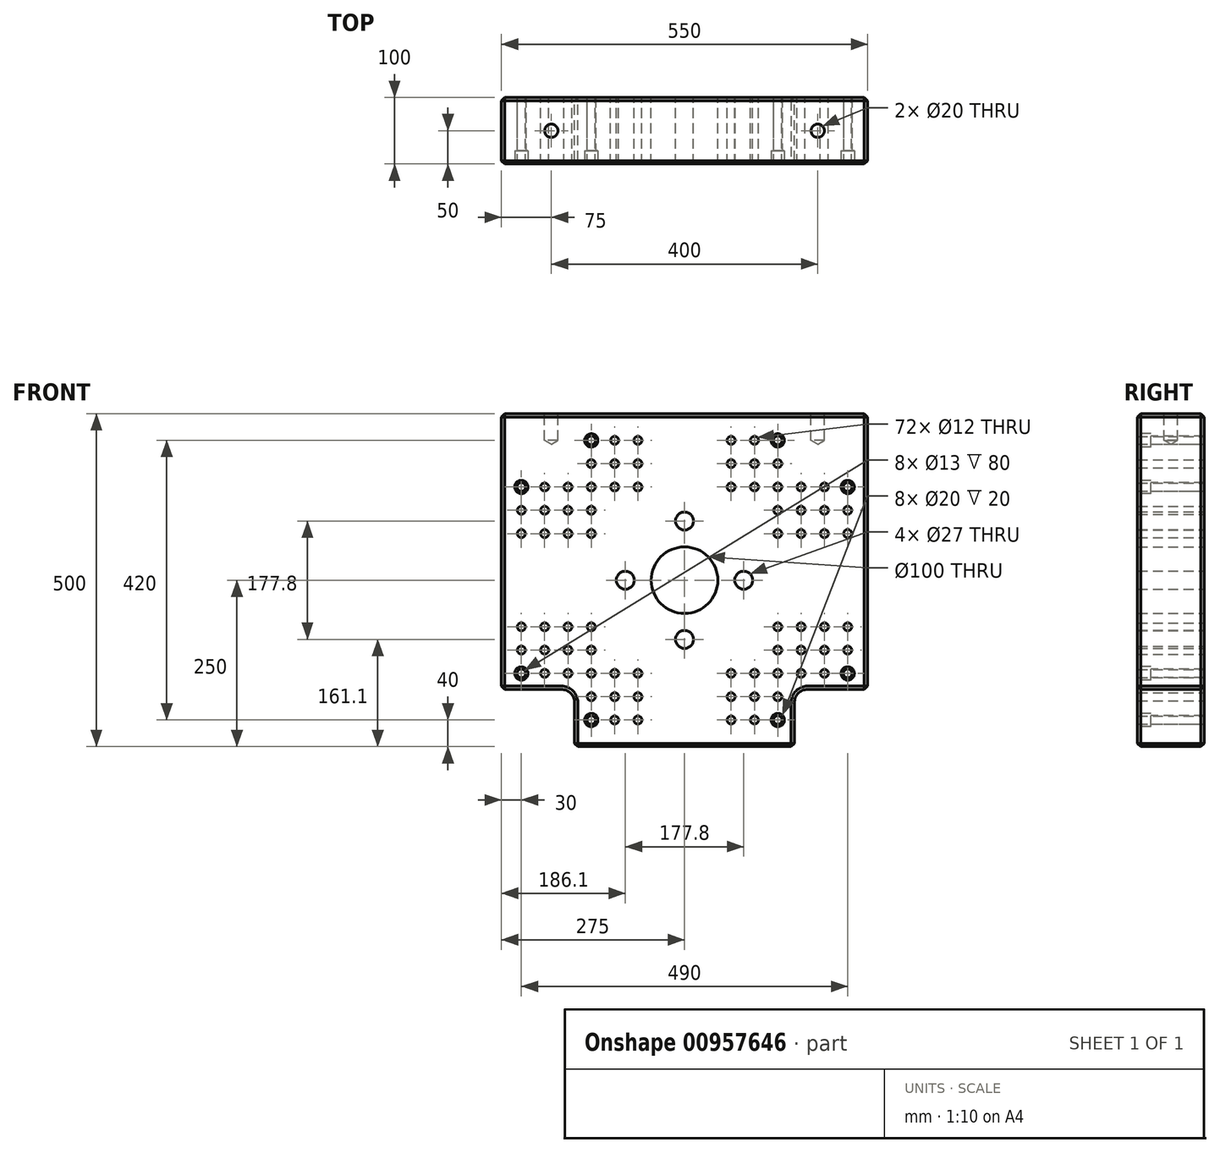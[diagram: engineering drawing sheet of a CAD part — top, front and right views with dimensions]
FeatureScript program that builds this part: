
annotation { "Feature Type Name" : "Feature", "Feature Type Description" : "" }
export const myFeature = defineFeature(function(context is Context, id is Id, definition is map)
    precondition{}
    {
        {
            var Q0;
            Q0=qCreatedBy(makeId("Front.planeOp"),FACE);
            var sketch = newSketch(context, id + "F0", { "sketchPlane" : qUnion([Q0])});
            skLineSegment(sketch, "E0", {"start": v(0, 0) * mm, "end": v(-219.59, 0) * mm, "construction": true});
            skLineSegment(sketch, "E1", {"start": v(0, 0) * mm, "end": v(0, -187.77) * mm, "construction": true});
            skLineSegment(sketch, "E2", {"start": v(-275, 250) * mm, "end": v(-275, -164) * mm});
            skLineSegment(sketch, "E3", {"start": v(-165, -250) * mm, "end": v(165, -250) * mm});
            skLineSegment(sketch, "E4", {"start": v(275, -164) * mm, "end": v(275, 250) * mm});
            skLineSegment(sketch, "E5", {"start": v(275, 250) * mm, "end": v(-275, 250) * mm});
            skLineSegment(sketch, "E6", {"start": v(-275, -164) * mm, "end": v(-185, -164) * mm});
            skLineSegment(sketch, "E7", {"start": v(-165, -184) * mm, "end": v(-165, -250) * mm});
            skLineSegment(sketch, "E8", {"start": v(165, -250) * mm, "end": v(165, -184) * mm});
            skLineSegment(sketch, "E9", {"start": v(185, -164) * mm, "end": v(275, -164) * mm});
            skCircle(sketch, "E10", {"center": v(0, 0) * mm, "radius": 50 * mm});
            skCircle(sketch, "E11", {"center": v(-140, 210) * mm, "radius": 6 * mm});
            skCircle(sketch, "E12.0.1.0", {"center": v(-140, 175) * mm, "radius": 6 * mm});
            skCircle(sketch, "E12.0.2.0", {"center": v(-140, 140) * mm, "radius": 6 * mm});
            skCircle(sketch, "E12.1.0.0", {"center": v(-105, 210) * mm, "radius": 6 * mm});
            skCircle(sketch, "E12.1.1.0", {"center": v(-105, 175) * mm, "radius": 6 * mm});
            skCircle(sketch, "E12.1.2.0", {"center": v(-105, 140) * mm, "radius": 6 * mm});
            skCircle(sketch, "E12.2.0.0", {"center": v(-70, 210) * mm, "radius": 6 * mm});
            skCircle(sketch, "E12.2.1.0", {"center": v(-70, 175) * mm, "radius": 6 * mm});
            skCircle(sketch, "E12.2.2.0", {"center": v(-70, 140) * mm, "radius": 6 * mm});
            skLineSegment(sketch, "E12.direction1", {"start": v(-140, 210) * mm, "end": v(-105, 210) * mm, "construction": true});
            skLineSegment(sketch, "E12.direction2", {"start": v(-140, 210) * mm, "end": v(-140, 175) * mm, "construction": true});
            skCircle(sketch, "E13.0.1.0", {"center": v(-140, 105) * mm, "radius": 6 * mm});
            skCircle(sketch, "E13.0.2.0", {"center": v(-140, 70) * mm, "radius": 6 * mm});
            skCircle(sketch, "E13.1.0.0", {"center": v(-175, 140) * mm, "radius": 6 * mm});
            skCircle(sketch, "E13.1.1.0", {"center": v(-175, 105) * mm, "radius": 6 * mm});
            skCircle(sketch, "E13.1.2.0", {"center": v(-175, 70) * mm, "radius": 6 * mm});
            skCircle(sketch, "E13.2.0.0", {"center": v(-210, 140) * mm, "radius": 6 * mm});
            skCircle(sketch, "E13.2.1.0", {"center": v(-210, 105) * mm, "radius": 6 * mm});
            skCircle(sketch, "E13.2.2.0", {"center": v(-210, 70) * mm, "radius": 6 * mm});
            skCircle(sketch, "E13.3.0.0", {"center": v(-245, 140) * mm, "radius": 6 * mm});
            skCircle(sketch, "E13.3.1.0", {"center": v(-245, 105) * mm, "radius": 6 * mm});
            skCircle(sketch, "E13.3.2.0", {"center": v(-245, 70) * mm, "radius": 6 * mm});
            skLineSegment(sketch, "E13.direction1", {"start": v(-140, 140) * mm, "end": v(-175, 140) * mm, "construction": true});
            skLineSegment(sketch, "E13.direction2", {"start": v(-140, 140) * mm, "end": v(-140, 105) * mm, "construction": true});
            skCircle(sketch, "E14.MirrorC", {"center": v(140, 210) * mm, "radius": 6 * mm});
            skCircle(sketch, "E15.MirrorC", {"center": v(140, 140) * mm, "radius": 6 * mm});
            skCircle(sketch, "E16.MirrorC", {"center": v(140, 175) * mm, "radius": 6 * mm});
            skCircle(sketch, "E17.MirrorC", {"center": v(140, 105) * mm, "radius": 6 * mm});
            skCircle(sketch, "E18.MirrorC", {"center": v(105, 210) * mm, "radius": 6 * mm});
            skCircle(sketch, "E19.MirrorC", {"center": v(175, 140) * mm, "radius": 6 * mm});
            skCircle(sketch, "E20.MirrorC", {"center": v(105, 140) * mm, "radius": 6 * mm});
            skCircle(sketch, "E21.MirrorC", {"center": v(105, 175) * mm, "radius": 6 * mm});
            skCircle(sketch, "E22.MirrorC", {"center": v(210, 105) * mm, "radius": 6 * mm});
            skCircle(sketch, "E23.MirrorC", {"center": v(210, 70) * mm, "radius": 6 * mm});
            skCircle(sketch, "E24.MirrorC", {"center": v(175, 105) * mm, "radius": 6 * mm});
            skCircle(sketch, "E25.MirrorC", {"center": v(70, 210) * mm, "radius": 6 * mm});
            skCircle(sketch, "E26.MirrorC", {"center": v(245, 70) * mm, "radius": 6 * mm});
            skCircle(sketch, "E27.MirrorC", {"center": v(210, 140) * mm, "radius": 6 * mm});
            skCircle(sketch, "E28.MirrorC", {"center": v(245, 140) * mm, "radius": 6 * mm});
            skCircle(sketch, "E29.MirrorC", {"center": v(140, 70) * mm, "radius": 6 * mm});
            skCircle(sketch, "E30.MirrorC", {"center": v(70, 175) * mm, "radius": 6 * mm});
            skCircle(sketch, "E31.MirrorC", {"center": v(175, 70) * mm, "radius": 6 * mm});
            skCircle(sketch, "E32.MirrorC", {"center": v(245, 105) * mm, "radius": 6 * mm});
            skCircle(sketch, "E33.MirrorC", {"center": v(70, 140) * mm, "radius": 6 * mm});
            skLineSegment(sketch, "E34.MirrorCS", {"start": v(140, 140) * mm, "end": v(140, 105) * mm, "construction": true});
            skLineSegment(sketch, "E35.MirrorCS", {"start": v(140, 140) * mm, "end": v(175, 140) * mm, "construction": true});
            skLineSegment(sketch, "E36.MirrorCS", {"start": v(140, 210) * mm, "end": v(140, 175) * mm, "construction": true});
            skLineSegment(sketch, "E37.MirrorCS", {"start": v(140, 210) * mm, "end": v(105, 210) * mm, "construction": true});
            skCircle(sketch, "E38.MirrorC", {"center": v(-140, -210) * mm, "radius": 6 * mm});
            skCircle(sketch, "E39.MirrorC", {"center": v(-140, -140) * mm, "radius": 6 * mm});
            skCircle(sketch, "E40.MirrorC", {"center": v(140, -140) * mm, "radius": 6 * mm});
            skCircle(sketch, "E41.MirrorC", {"center": v(140, -210) * mm, "radius": 6 * mm});
            skCircle(sketch, "E42.MirrorC", {"center": v(-175, -140) * mm, "radius": 6 * mm});
            skCircle(sketch, "E43.MirrorC", {"center": v(105, -210) * mm, "radius": 6 * mm});
            skCircle(sketch, "E44.MirrorC", {"center": v(-105, -210) * mm, "radius": 6 * mm});
            skCircle(sketch, "E45.MirrorC", {"center": v(140, -105) * mm, "radius": 6 * mm});
            skCircle(sketch, "E46.MirrorC", {"center": v(140, -175) * mm, "radius": 6 * mm});
            skCircle(sketch, "E47.MirrorC", {"center": v(175, -140) * mm, "radius": 6 * mm});
            skCircle(sketch, "E48.MirrorC", {"center": v(-140, -105) * mm, "radius": 6 * mm});
            skCircle(sketch, "E49.MirrorC", {"center": v(-140, -175) * mm, "radius": 6 * mm});
            skCircle(sketch, "E50.MirrorC", {"center": v(245, -105) * mm, "radius": 6 * mm});
            skLineSegment(sketch, "E51.MirrorCS", {"start": v(-140, -210) * mm, "end": v(-105, -210) * mm, "construction": true});
            skCircle(sketch, "E52.MirrorC", {"center": v(-175, -70) * mm, "radius": 6 * mm});
            skCircle(sketch, "E53.MirrorC", {"center": v(-210, -140) * mm, "radius": 6 * mm});
            skCircle(sketch, "E54.MirrorC", {"center": v(70, -175) * mm, "radius": 6 * mm});
            skCircle(sketch, "E55.MirrorC", {"center": v(-105, -140) * mm, "radius": 6 * mm});
            skCircle(sketch, "E56.MirrorC", {"center": v(175, -105) * mm, "radius": 6 * mm});
            skCircle(sketch, "E57.MirrorC", {"center": v(-105, -175) * mm, "radius": 6 * mm});
            skCircle(sketch, "E58.MirrorC", {"center": v(105, -140) * mm, "radius": 6 * mm});
            skCircle(sketch, "E59.MirrorC", {"center": v(-175, -105) * mm, "radius": 6 * mm});
            skCircle(sketch, "E60.MirrorC", {"center": v(245, -140) * mm, "radius": 6 * mm});
            skCircle(sketch, "E61.MirrorC", {"center": v(-245, -140) * mm, "radius": 6 * mm});
            skCircle(sketch, "E62.MirrorC", {"center": v(70, -140) * mm, "radius": 6 * mm});
            skCircle(sketch, "E63.MirrorC", {"center": v(-70, -175) * mm, "radius": 6 * mm});
            skCircle(sketch, "E64.MirrorC", {"center": v(-210, -105) * mm, "radius": 6 * mm});
            skCircle(sketch, "E65.MirrorC", {"center": v(70, -210) * mm, "radius": 6 * mm});
            skCircle(sketch, "E66.MirrorC", {"center": v(-70, -210) * mm, "radius": 6 * mm});
            skCircle(sketch, "E67.MirrorC", {"center": v(-140, -70) * mm, "radius": 6 * mm});
            skCircle(sketch, "E68.MirrorC", {"center": v(-245, -105) * mm, "radius": 6 * mm});
            skCircle(sketch, "E69.MirrorC", {"center": v(245, -70) * mm, "radius": 6 * mm});
            skCircle(sketch, "E70.MirrorC", {"center": v(175, -70) * mm, "radius": 6 * mm});
            skCircle(sketch, "E71.MirrorC", {"center": v(-245, -70) * mm, "radius": 6 * mm});
            skCircle(sketch, "E72.MirrorC", {"center": v(210, -140) * mm, "radius": 6 * mm});
            skCircle(sketch, "E73.MirrorC", {"center": v(210, -70) * mm, "radius": 6 * mm});
            skCircle(sketch, "E74.MirrorC", {"center": v(-70, -140) * mm, "radius": 6 * mm});
            skCircle(sketch, "E75.MirrorC", {"center": v(210, -105) * mm, "radius": 6 * mm});
            skCircle(sketch, "E76.MirrorC", {"center": v(140, -70) * mm, "radius": 6 * mm});
            skCircle(sketch, "E77.MirrorC", {"center": v(-210, -70) * mm, "radius": 6 * mm});
            skCircle(sketch, "E78.MirrorC", {"center": v(105, -175) * mm, "radius": 6 * mm});
            skLineSegment(sketch, "E79.MirrorCS", {"start": v(-140, -140) * mm, "end": v(-175, -140) * mm, "construction": true});
            skLineSegment(sketch, "E80.MirrorCS", {"start": v(-140, -210) * mm, "end": v(-140, -175) * mm, "construction": true});
            skLineSegment(sketch, "E81.MirrorCS", {"start": v(140, -210) * mm, "end": v(105, -210) * mm, "construction": true});
            skLineSegment(sketch, "E82.MirrorCS", {"start": v(140, -140) * mm, "end": v(140, -105) * mm, "construction": true});
            skLineSegment(sketch, "E83.MirrorCS", {"start": v(140, -210) * mm, "end": v(140, -175) * mm, "construction": true});
            skLineSegment(sketch, "E84.MirrorCS", {"start": v(-140, -140) * mm, "end": v(-140, -105) * mm, "construction": true});
            skLineSegment(sketch, "E85.MirrorCS", {"start": v(140, -140) * mm, "end": v(175, -140) * mm, "construction": true});
            skPoint(sketch, "E86.visualSharp", {"position": v(-165, -164) * mm});
            skArc(sketch, "E86.filletArc", {"start": v(-165, -184) * mm, "mid": v(-170.86, -169.86) * mm, "end": v(-185, -164) * mm});
            skPoint(sketch, "E87.visualSharp", {"position": v(165, -164) * mm});
            skArc(sketch, "E87.filletArc", {"start": v(185, -164) * mm, "mid": v(170.86, -169.86) * mm, "end": v(165, -184) * mm});
            skCircle(sketch, "E88", {"center": v(88.9, 0) * mm, "radius": 13.5 * mm});
            skCircle(sketch, "E89", {"center": v(0, 88.9) * mm, "radius": 13.5 * mm});
            skCircle(sketch, "E90", {"center": v(-88.9, 0) * mm, "radius": 13.5 * mm});
            skCircle(sketch, "E91", {"center": v(0, -88.9) * mm, "radius": 13.5 * mm});
            skSolve(sketch);
        }
        {
            var Q0;
            Q0 = qSketchRegion(id + "F0", true);
            extrude(context, id + "F1", {"entities" : qUnion([Q0]), "depth" : 100 * mm, "offsetDistance" : 25 * mm});
        }
        {
            var Q0;
            Q0=makeQuery(id+"F1.opExtrude","CAP_FACE",FACE,{"disambiguationData":[OSD([sQuery(id+"F0.wireOp",EDGE,"E2"),sQuery(id+"F0.wireOp",EDGE,"E3"),sQuery(id+"F0.wireOp",EDGE,"E4"),sQuery(id+"F0.wireOp",EDGE,"E5"),sQuery(id+"F0.wireOp",EDGE,"E6"),sQuery(id+"F0.wireOp",EDGE,"E7"),sQuery(id+"F0.wireOp",EDGE,"E8"),sQuery(id+"F0.wireOp",EDGE,"E9"),sQuery(id+"F0.wireOp",EDGE,"E10"),sQuery(id+"F0.wireOp",EDGE,"E11"),sQuery(id+"F0.wireOp",EDGE,"E12.0.1.0"),sQuery(id+"F0.wireOp",EDGE,"E12.0.2.0"),sQuery(id+"F0.wireOp",EDGE,"E12.1.0.0"),sQuery(id+"F0.wireOp",EDGE,"E12.1.1.0"),sQuery(id+"F0.wireOp",EDGE,"E12.1.2.0"),sQuery(id+"F0.wireOp",EDGE,"E12.2.0.0"),sQuery(id+"F0.wireOp",EDGE,"E12.2.1.0"),sQuery(id+"F0.wireOp",EDGE,"E12.2.2.0"),sQuery(id+"F0.wireOp",EDGE,"E13.0.1.0"),sQuery(id+"F0.wireOp",EDGE,"E13.0.2.0"),sQuery(id+"F0.wireOp",EDGE,"E13.0.3.0"),sQuery(id+"F0.wireOp",EDGE,"E13.1.0.0"),sQuery(id+"F0.wireOp",EDGE,"E13.1.1.0"),sQuery(id+"F0.wireOp",EDGE,"E13.1.2.0"),sQuery(id+"F0.wireOp",EDGE,"E13.1.3.0"),sQuery(id+"F0.wireOp",EDGE,"E13.2.0.0"),sQuery(id+"F0.wireOp",EDGE,"E13.2.1.0"),sQuery(id+"F0.wireOp",EDGE,"E13.2.2.0"),sQuery(id+"F0.wireOp",EDGE,"E13.2.3.0"),sQuery(id+"F0.wireOp",EDGE,"E13.3.0.0"),sQuery(id+"F0.wireOp",EDGE,"E13.3.1.0"),sQuery(id+"F0.wireOp",EDGE,"E13.3.2.0"),sQuery(id+"F0.wireOp",EDGE,"E13.3.3.0"),sQuery(id+"F0.wireOp",EDGE,"E14.MirrorC"),sQuery(id+"F0.wireOp",EDGE,"E15.MirrorC"),sQuery(id+"F0.wireOp",EDGE,"E16.MirrorC"),sQuery(id+"F0.wireOp",EDGE,"E17.MirrorC"),sQuery(id+"F0.wireOp",EDGE,"E18.MirrorC"),sQuery(id+"F0.wireOp",EDGE,"E19.MirrorC"),sQuery(id+"F0.wireOp",EDGE,"97c1720e-c5f1-4ad0-973d-ed2b327d89556.MirrorC"),sQuery(id+"F0.wireOp",EDGE,"E20.MirrorC"),sQuery(id+"F0.wireOp",EDGE,"97c1720e-c5f1-4ad0-973d-ed2b327d89558.MirrorC"),sQuery(id+"F0.wireOp",EDGE,"E21.MirrorC"),sQuery(id+"F0.wireOp",EDGE,"E150.MirrorC"),sQuery(id+"F0.wireOp",EDGE,"E22.MirrorC"),sQuery(id+"F0.wireOp",EDGE,"E23.MirrorC"),sQuery(id+"F0.wireOp",EDGE,"E24.MirrorC"),sQuery(id+"F0.wireOp",EDGE,"E25.MirrorC"),sQuery(id+"F0.wireOp",EDGE,"E26.MirrorC"),sQuery(id+"F0.wireOp",EDGE,"E27.MirrorC"),sQuery(id+"F0.wireOp",EDGE,"E28.MirrorC"),sQuery(id+"F0.wireOp",EDGE,"E29.MirrorC"),sQuery(id+"F0.wireOp",EDGE,"E30.MirrorC"),sQuery(id+"F0.wireOp",EDGE,"E160.MirrorC"),sQuery(id+"F0.wireOp",EDGE,"E31.MirrorC"),sQuery(id+"F0.wireOp",EDGE,"E32.MirrorC"),sQuery(id+"F0.wireOp",EDGE,"E33.MirrorC"),sQuery(id+"F0.wireOp",EDGE,"E38.MirrorC"),sQuery(id+"F0.wireOp",EDGE,"E39.MirrorC"),sQuery(id+"F0.wireOp",EDGE,"E40.MirrorC"),sQuery(id+"F0.wireOp",EDGE,"E41.MirrorC"),sQuery(id+"F0.wireOp",EDGE,"E42.MirrorC"),sQuery(id+"F0.wireOp",EDGE,"E43.MirrorC"),sQuery(id+"F0.wireOp",EDGE,"E44.MirrorC"),sQuery(id+"F0.wireOp",EDGE,"E45.MirrorC"),sQuery(id+"F0.wireOp",EDGE,"E46.MirrorC"),sQuery(id+"F0.wireOp",EDGE,"E47.MirrorC"),sQuery(id+"F0.wireOp",EDGE,"E48.MirrorC"),sQuery(id+"F0.wireOp",EDGE,"E49.MirrorC"),sQuery(id+"F0.wireOp",EDGE,"E50.MirrorC"),sQuery(id+"F0.wireOp",EDGE,"E52.MirrorC"),sQuery(id+"F0.wireOp",EDGE,"E395.MirrorC"),sQuery(id+"F0.wireOp",EDGE,"E396.MirrorC"),sQuery(id+"F0.wireOp",EDGE,"E53.MirrorC"),sQuery(id+"F0.wireOp",EDGE,"E398.MirrorC"),sQuery(id+"F0.wireOp",EDGE,"E54.MirrorC"),sQuery(id+"F0.wireOp",EDGE,"E55.MirrorC"),sQuery(id+"F0.wireOp",EDGE,"E56.MirrorC"),sQuery(id+"F0.wireOp",EDGE,"E57.MirrorC"),sQuery(id+"F0.wireOp",EDGE,"E403.MirrorC"),sQuery(id+"F0.wireOp",EDGE,"E58.MirrorC"),sQuery(id+"F0.wireOp",EDGE,"E59.MirrorC"),sQuery(id+"F0.wireOp",EDGE,"E60.MirrorC"),sQuery(id+"F0.wireOp",EDGE,"E61.MirrorC"),sQuery(id+"F0.wireOp",EDGE,"E62.MirrorC"),sQuery(id+"F0.wireOp",EDGE,"E63.MirrorC"),sQuery(id+"F0.wireOp",EDGE,"E64.MirrorC"),sQuery(id+"F0.wireOp",EDGE,"E65.MirrorC"),sQuery(id+"F0.wireOp",EDGE,"E66.MirrorC"),sQuery(id+"F0.wireOp",EDGE,"E67.MirrorC"),sQuery(id+"F0.wireOp",EDGE,"E68.MirrorC"),sQuery(id+"F0.wireOp",EDGE,"E69.MirrorC"),sQuery(id+"F0.wireOp",EDGE,"E416.MirrorC"),sQuery(id+"F0.wireOp",EDGE,"E70.MirrorC"),sQuery(id+"F0.wireOp",EDGE,"E418.MirrorC"),sQuery(id+"F0.wireOp",EDGE,"E419.MirrorC"),sQuery(id+"F0.wireOp",EDGE,"E71.MirrorC"),sQuery(id+"F0.wireOp",EDGE,"E72.MirrorC"),sQuery(id+"F0.wireOp",EDGE,"E73.MirrorC"),sQuery(id+"F0.wireOp",EDGE,"E423.MirrorC"),sQuery(id+"F0.wireOp",EDGE,"E74.MirrorC"),sQuery(id+"F0.wireOp",EDGE,"E75.MirrorC"),sQuery(id+"F0.wireOp",EDGE,"E76.MirrorC"),sQuery(id+"F0.wireOp",EDGE,"E77.MirrorC"),sQuery(id+"F0.wireOp",EDGE,"E78.MirrorC"),sQuery(id+"F0.wireOp",EDGE,"E86.filletArc"),sQuery(id+"F0.wireOp",EDGE,"E87.filletArc"),sQuery(id+"F0.wireOp",EDGE,"E88"),sQuery(id+"F0.wireOp",EDGE,"E89"),sQuery(id+"F0.wireOp",EDGE,"E90"),sQuery(id+"F0.wireOp",EDGE,"E91")])],"isStart":false});
            var sketch = newSketch(context, id + "F2", { "sketchPlane" : qUnion([Q0])});
            skPoint(sketch, "E92", {"position": v(-245, 140) * mm});
            skPoint(sketch, "E93", {"position": v(-245, -140) * mm});
            skPoint(sketch, "E94", {"position": v(245, -140) * mm});
            skPoint(sketch, "E95", {"position": v(245, 140) * mm});
            skPoint(sketch, "E96", {"position": v(-140, 210) * mm});
            skPoint(sketch, "E97", {"position": v(70, 210) * mm});
            skPoint(sketch, "E98", {"position": v(-140, -210) * mm});
            skPoint(sketch, "E99", {"position": v(140, -210) * mm});
            skPoint(sketch, "E100", {"position": v(140, 210) * mm});
            skSolve(sketch);
        }
        {
            var Q0;
            Q0=sQuery(id+"F2.wireOp",VERTEX,"E92");
            var Q1;
            Q1=sQuery(id+"F2.wireOp",VERTEX,"E95");
            var Q2;
            Q2=sQuery(id+"F2.wireOp",VERTEX,"E94");
            var Q3;
            Q3=sQuery(id+"F2.wireOp",VERTEX,"E93");
            var Q4;
            Q4=sQuery(id+"F2.wireOp",VERTEX,"E96");
            var Q5;
            Q5=sQuery(id+"F2.wireOp",VERTEX,"E99");
            var Q6;
            Q6=sQuery(id+"F2.wireOp",VERTEX,"E98");
            var Q7;
            Q7=sQuery(id+"F2.wireOp",VERTEX,"E100");
            var Q8;
            Q8=makeQuery(id+"F1.opExtrude","SWEPT_BODY",BODY,{"disambiguationData":[OSD([sQuery(id+"F0.wireOp",EDGE,"E2"),sQuery(id+"F0.wireOp",EDGE,"E3"),sQuery(id+"F0.wireOp",EDGE,"E4"),sQuery(id+"F0.wireOp",EDGE,"E5"),sQuery(id+"F0.wireOp",EDGE,"E6"),sQuery(id+"F0.wireOp",EDGE,"E7"),sQuery(id+"F0.wireOp",EDGE,"E8"),sQuery(id+"F0.wireOp",EDGE,"E9"),sQuery(id+"F0.wireOp",EDGE,"E10"),sQuery(id+"F0.wireOp",EDGE,"E11"),sQuery(id+"F0.wireOp",EDGE,"E12.0.1.0"),sQuery(id+"F0.wireOp",EDGE,"E12.0.2.0"),sQuery(id+"F0.wireOp",EDGE,"E12.1.0.0"),sQuery(id+"F0.wireOp",EDGE,"E12.1.1.0"),sQuery(id+"F0.wireOp",EDGE,"E12.1.2.0"),sQuery(id+"F0.wireOp",EDGE,"E12.2.0.0"),sQuery(id+"F0.wireOp",EDGE,"E12.2.1.0"),sQuery(id+"F0.wireOp",EDGE,"E12.2.2.0"),sQuery(id+"F0.wireOp",EDGE,"E13.0.1.0"),sQuery(id+"F0.wireOp",EDGE,"E13.0.2.0"),sQuery(id+"F0.wireOp",EDGE,"E13.0.3.0"),sQuery(id+"F0.wireOp",EDGE,"E13.1.0.0"),sQuery(id+"F0.wireOp",EDGE,"E13.1.1.0"),sQuery(id+"F0.wireOp",EDGE,"E13.1.2.0"),sQuery(id+"F0.wireOp",EDGE,"E13.1.3.0"),sQuery(id+"F0.wireOp",EDGE,"E13.2.0.0"),sQuery(id+"F0.wireOp",EDGE,"E13.2.1.0"),sQuery(id+"F0.wireOp",EDGE,"E13.2.2.0"),sQuery(id+"F0.wireOp",EDGE,"E13.2.3.0"),sQuery(id+"F0.wireOp",EDGE,"E13.3.0.0"),sQuery(id+"F0.wireOp",EDGE,"E13.3.1.0"),sQuery(id+"F0.wireOp",EDGE,"E13.3.2.0"),sQuery(id+"F0.wireOp",EDGE,"E13.3.3.0"),sQuery(id+"F0.wireOp",EDGE,"E14.MirrorC"),sQuery(id+"F0.wireOp",EDGE,"E15.MirrorC"),sQuery(id+"F0.wireOp",EDGE,"E16.MirrorC"),sQuery(id+"F0.wireOp",EDGE,"E17.MirrorC"),sQuery(id+"F0.wireOp",EDGE,"E18.MirrorC"),sQuery(id+"F0.wireOp",EDGE,"E19.MirrorC"),sQuery(id+"F0.wireOp",EDGE,"97c1720e-c5f1-4ad0-973d-ed2b327d89556.MirrorC"),sQuery(id+"F0.wireOp",EDGE,"E20.MirrorC"),sQuery(id+"F0.wireOp",EDGE,"97c1720e-c5f1-4ad0-973d-ed2b327d89558.MirrorC"),sQuery(id+"F0.wireOp",EDGE,"E21.MirrorC"),sQuery(id+"F0.wireOp",EDGE,"E150.MirrorC"),sQuery(id+"F0.wireOp",EDGE,"E22.MirrorC"),sQuery(id+"F0.wireOp",EDGE,"E23.MirrorC"),sQuery(id+"F0.wireOp",EDGE,"E24.MirrorC"),sQuery(id+"F0.wireOp",EDGE,"E25.MirrorC"),sQuery(id+"F0.wireOp",EDGE,"E26.MirrorC"),sQuery(id+"F0.wireOp",EDGE,"E27.MirrorC"),sQuery(id+"F0.wireOp",EDGE,"E28.MirrorC"),sQuery(id+"F0.wireOp",EDGE,"E29.MirrorC"),sQuery(id+"F0.wireOp",EDGE,"E30.MirrorC"),sQuery(id+"F0.wireOp",EDGE,"E160.MirrorC"),sQuery(id+"F0.wireOp",EDGE,"E31.MirrorC"),sQuery(id+"F0.wireOp",EDGE,"E32.MirrorC"),sQuery(id+"F0.wireOp",EDGE,"E33.MirrorC"),sQuery(id+"F0.wireOp",EDGE,"E38.MirrorC"),sQuery(id+"F0.wireOp",EDGE,"E39.MirrorC"),sQuery(id+"F0.wireOp",EDGE,"E40.MirrorC"),sQuery(id+"F0.wireOp",EDGE,"E41.MirrorC"),sQuery(id+"F0.wireOp",EDGE,"E42.MirrorC"),sQuery(id+"F0.wireOp",EDGE,"E43.MirrorC"),sQuery(id+"F0.wireOp",EDGE,"E44.MirrorC"),sQuery(id+"F0.wireOp",EDGE,"E45.MirrorC"),sQuery(id+"F0.wireOp",EDGE,"E46.MirrorC"),sQuery(id+"F0.wireOp",EDGE,"E47.MirrorC"),sQuery(id+"F0.wireOp",EDGE,"E48.MirrorC"),sQuery(id+"F0.wireOp",EDGE,"E49.MirrorC"),sQuery(id+"F0.wireOp",EDGE,"E50.MirrorC"),sQuery(id+"F0.wireOp",EDGE,"E52.MirrorC"),sQuery(id+"F0.wireOp",EDGE,"E395.MirrorC"),sQuery(id+"F0.wireOp",EDGE,"E396.MirrorC"),sQuery(id+"F0.wireOp",EDGE,"E53.MirrorC"),sQuery(id+"F0.wireOp",EDGE,"E398.MirrorC"),sQuery(id+"F0.wireOp",EDGE,"E54.MirrorC"),sQuery(id+"F0.wireOp",EDGE,"E55.MirrorC"),sQuery(id+"F0.wireOp",EDGE,"E56.MirrorC"),sQuery(id+"F0.wireOp",EDGE,"E57.MirrorC"),sQuery(id+"F0.wireOp",EDGE,"E403.MirrorC"),sQuery(id+"F0.wireOp",EDGE,"E58.MirrorC"),sQuery(id+"F0.wireOp",EDGE,"E59.MirrorC"),sQuery(id+"F0.wireOp",EDGE,"E60.MirrorC"),sQuery(id+"F0.wireOp",EDGE,"E61.MirrorC"),sQuery(id+"F0.wireOp",EDGE,"E62.MirrorC"),sQuery(id+"F0.wireOp",EDGE,"E63.MirrorC"),sQuery(id+"F0.wireOp",EDGE,"E64.MirrorC"),sQuery(id+"F0.wireOp",EDGE,"E65.MirrorC"),sQuery(id+"F0.wireOp",EDGE,"E66.MirrorC"),sQuery(id+"F0.wireOp",EDGE,"E67.MirrorC"),sQuery(id+"F0.wireOp",EDGE,"E68.MirrorC"),sQuery(id+"F0.wireOp",EDGE,"E69.MirrorC"),sQuery(id+"F0.wireOp",EDGE,"E416.MirrorC"),sQuery(id+"F0.wireOp",EDGE,"E70.MirrorC"),sQuery(id+"F0.wireOp",EDGE,"E418.MirrorC"),sQuery(id+"F0.wireOp",EDGE,"E419.MirrorC"),sQuery(id+"F0.wireOp",EDGE,"E71.MirrorC"),sQuery(id+"F0.wireOp",EDGE,"E72.MirrorC"),sQuery(id+"F0.wireOp",EDGE,"E73.MirrorC"),sQuery(id+"F0.wireOp",EDGE,"E423.MirrorC"),sQuery(id+"F0.wireOp",EDGE,"E74.MirrorC"),sQuery(id+"F0.wireOp",EDGE,"E75.MirrorC"),sQuery(id+"F0.wireOp",EDGE,"E76.MirrorC"),sQuery(id+"F0.wireOp",EDGE,"E77.MirrorC"),sQuery(id+"F0.wireOp",EDGE,"E78.MirrorC"),sQuery(id+"F0.wireOp",EDGE,"E86.filletArc"),sQuery(id+"F0.wireOp",EDGE,"E87.filletArc"),sQuery(id+"F0.wireOp",EDGE,"E88"),sQuery(id+"F0.wireOp",EDGE,"E89"),sQuery(id+"F0.wireOp",EDGE,"E90"),sQuery(id+"F0.wireOp",EDGE,"E91")])]});
            hole(context, id + "F3", {"style" : HoleStyle.C_BORE, "endStyle" : HoleEndStyle.THROUGH, "holeDiameter" : 13 * mm, "cBoreDiameter" : 20 * mm, "cBoreDepth" : 20 * mm, "majorDiameter" : 5 * mm, "isTappedThrough" : true, "tappedDepth" : 12 * mm, "tapClearance" : 3, "locations" : qUnion([Q0, Q1, Q2, Q3, Q4, Q5, Q6, Q7]), "scope" : qUnion([Q8])});
        }
        {
            var Q0;
            Q0=makeQuery(id+"F1.opExtrude","CAP_EDGE",EDGE,{"disambiguationData":[OSD([sQuery(id+"F0.wireOp",EDGE,"E2")])],"isStart":false});
            var Q1;
            Q1=makeQuery(id+"F1.opExtrude","CAP_EDGE",EDGE,{"disambiguationData":[OSD([sQuery(id+"F0.wireOp",EDGE,"E5")])],"isStart":false});
            var Q2;
            Q2=makeQuery(id+"F1.opExtrude","CAP_EDGE",EDGE,{"disambiguationData":[OSD([sQuery(id+"F0.wireOp",EDGE,"E4")])],"isStart":false});
            var Q3;
            Q3=makeQuery(id+"F1.opExtrude","CAP_EDGE",EDGE,{"disambiguationData":[OSD([sQuery(id+"F0.wireOp",EDGE,"E9")])],"isStart":false});
            var Q4;
            Q4=makeQuery(id+"F1.opExtrude","CAP_EDGE",EDGE,{"disambiguationData":[OSD([sQuery(id+"F0.wireOp",EDGE,"E3")])],"isStart":false});
            var Q5;
            Q5=makeQuery(id+"F1.opExtrude","CAP_EDGE",EDGE,{"disambiguationData":[OSD([sQuery(id+"F0.wireOp",EDGE,"E7")])],"isStart":false});
            var Q6;
            Q6=makeQuery(id+"F1.opExtrude","CAP_EDGE",EDGE,{"disambiguationData":[OSD([sQuery(id+"F0.wireOp",EDGE,"E4")])],"isStart":true});
            var Q7;
            Q7=makeQuery(id+"F1.opExtrude","CAP_EDGE",EDGE,{"disambiguationData":[OSD([sQuery(id+"F0.wireOp",EDGE,"E5")])],"isStart":true});
            var Q8;
            Q8=makeQuery(id+"F1.opExtrude","SWEPT_EDGE",EDGE,{"disambiguationData":[OSD([sQuery(id+"F0.wireOp",EDGE,"E4"),sQuery(id+"F0.wireOp",EDGE,"E5")])]});
            var Q9;
            Q9=makeQuery(id+"F1.opExtrude","CAP_EDGE",EDGE,{"disambiguationData":[OSD([sQuery(id+"F0.wireOp",EDGE,"E9")])],"isStart":true});
            var Q10;
            Q10=makeQuery(id+"F1.opExtrude","CAP_EDGE",EDGE,{"disambiguationData":[OSD([sQuery(id+"F0.wireOp",EDGE,"E3")])],"isStart":true});
            var Q11;
            Q11=makeQuery(id+"F1.opExtrude","CAP_EDGE",EDGE,{"disambiguationData":[OSD([sQuery(id+"F0.wireOp",EDGE,"E86.filletArc")])],"isStart":true});
            var Q12;
            Q12=makeQuery(id+"F1.opExtrude","SWEPT_EDGE",EDGE,{"disambiguationData":[OSD([sQuery(id+"F0.wireOp",EDGE,"E2"),sQuery(id+"F0.wireOp",EDGE,"E6")])]});
            var Q13;
            Q13=makeQuery(id+"F1.opExtrude","CAP_EDGE",EDGE,{"disambiguationData":[OSD([sQuery(id+"F0.wireOp",EDGE,"E2")])],"isStart":true});
            var Q14;
            Q14=makeQuery(id+"F1.opExtrude","SWEPT_EDGE",EDGE,{"disambiguationData":[OSD([sQuery(id+"F0.wireOp",EDGE,"E3"),sQuery(id+"F0.wireOp",EDGE,"E7")])]});
            var Q15;
            Q15=makeQuery(id+"F1.opExtrude","SWEPT_EDGE",EDGE,{"disambiguationData":[OSD([sQuery(id+"F0.wireOp",EDGE,"E3"),sQuery(id+"F0.wireOp",EDGE,"E8")])]});
            var Q16;
            Q16=makeQuery(id+"F1.opExtrude","SWEPT_EDGE",EDGE,{"disambiguationData":[OSD([sQuery(id+"F0.wireOp",EDGE,"E4"),sQuery(id+"F0.wireOp",EDGE,"E9")])]});
            var Q17;
            Q17=makeQuery(id+"F1.opExtrude","SWEPT_EDGE",EDGE,{"disambiguationData":[OSD([sQuery(id+"F0.wireOp",EDGE,"E2"),sQuery(id+"F0.wireOp",EDGE,"E5")])]});
            chamfer(context, id + "F4", {"entities" : qUnion([Q0, Q1, Q2, Q3, Q4, Q5, Q6, Q7, Q8, Q9, Q10, Q11, Q12, Q13, Q14, Q15, Q16, Q17]), "width" : 5 * mm, "tangentPropagation" : true});
        }
        {
            var Q0;
            Q0=makeQuery(id+"F1.opExtrude","SWEPT_FACE",FACE,{"disambiguationData":[OSD([sQuery(id+"F0.wireOp",EDGE,"E5")])]});
            var sketch = newSketch(context, id + "F5", { "sketchPlane" : qUnion([Q0])});
            skLineSegment(sketch, "E101", {"start": v(0, -5) * mm, "end": v(0, -95) * mm, "construction": true});
            skLineSegment(sketch, "E102", {"start": v(0, -50) * mm, "end": v(-102.82, -50) * mm, "construction": true});
            skPoint(sketch, "E103", {"position": v(-200, -50) * mm});
            skPoint(sketch, "E104", {"position": v(200, -50) * mm});
            skSolve(sketch);
        }
        {
            var Q0;
            Q0=sQuery(id+"F5.wireOp",VERTEX,"E103");
            var Q1;
            Q1=sQuery(id+"F5.wireOp",VERTEX,"E104");
            var Q2;
            Q2=makeQuery(id+"F1.opExtrude","SWEPT_BODY",BODY,{"disambiguationData":[OSD([sQuery(id+"F0.wireOp",EDGE,"E2"),sQuery(id+"F0.wireOp",EDGE,"E3"),sQuery(id+"F0.wireOp",EDGE,"E4"),sQuery(id+"F0.wireOp",EDGE,"E5"),sQuery(id+"F0.wireOp",EDGE,"E6"),sQuery(id+"F0.wireOp",EDGE,"E7"),sQuery(id+"F0.wireOp",EDGE,"E8"),sQuery(id+"F0.wireOp",EDGE,"E9"),sQuery(id+"F0.wireOp",EDGE,"E10"),sQuery(id+"F0.wireOp",EDGE,"E11"),sQuery(id+"F0.wireOp",EDGE,"E12.0.1.0"),sQuery(id+"F0.wireOp",EDGE,"E12.0.2.0"),sQuery(id+"F0.wireOp",EDGE,"E12.1.0.0"),sQuery(id+"F0.wireOp",EDGE,"E12.1.1.0"),sQuery(id+"F0.wireOp",EDGE,"E12.1.2.0"),sQuery(id+"F0.wireOp",EDGE,"E12.2.0.0"),sQuery(id+"F0.wireOp",EDGE,"E12.2.1.0"),sQuery(id+"F0.wireOp",EDGE,"E12.2.2.0"),sQuery(id+"F0.wireOp",EDGE,"E13.0.1.0"),sQuery(id+"F0.wireOp",EDGE,"E13.0.2.0"),sQuery(id+"F0.wireOp",EDGE,"E13.0.3.0"),sQuery(id+"F0.wireOp",EDGE,"E13.1.0.0"),sQuery(id+"F0.wireOp",EDGE,"E13.1.1.0"),sQuery(id+"F0.wireOp",EDGE,"E13.1.2.0"),sQuery(id+"F0.wireOp",EDGE,"E13.1.3.0"),sQuery(id+"F0.wireOp",EDGE,"E13.2.0.0"),sQuery(id+"F0.wireOp",EDGE,"E13.2.1.0"),sQuery(id+"F0.wireOp",EDGE,"E13.2.2.0"),sQuery(id+"F0.wireOp",EDGE,"E13.2.3.0"),sQuery(id+"F0.wireOp",EDGE,"E13.3.0.0"),sQuery(id+"F0.wireOp",EDGE,"E13.3.1.0"),sQuery(id+"F0.wireOp",EDGE,"E13.3.2.0"),sQuery(id+"F0.wireOp",EDGE,"E13.3.3.0"),sQuery(id+"F0.wireOp",EDGE,"E14.MirrorC"),sQuery(id+"F0.wireOp",EDGE,"E15.MirrorC"),sQuery(id+"F0.wireOp",EDGE,"E16.MirrorC"),sQuery(id+"F0.wireOp",EDGE,"E17.MirrorC"),sQuery(id+"F0.wireOp",EDGE,"E18.MirrorC"),sQuery(id+"F0.wireOp",EDGE,"E19.MirrorC"),sQuery(id+"F0.wireOp",EDGE,"97c1720e-c5f1-4ad0-973d-ed2b327d89556.MirrorC"),sQuery(id+"F0.wireOp",EDGE,"E20.MirrorC"),sQuery(id+"F0.wireOp",EDGE,"97c1720e-c5f1-4ad0-973d-ed2b327d89558.MirrorC"),sQuery(id+"F0.wireOp",EDGE,"E21.MirrorC"),sQuery(id+"F0.wireOp",EDGE,"E150.MirrorC"),sQuery(id+"F0.wireOp",EDGE,"E22.MirrorC"),sQuery(id+"F0.wireOp",EDGE,"E23.MirrorC"),sQuery(id+"F0.wireOp",EDGE,"E24.MirrorC"),sQuery(id+"F0.wireOp",EDGE,"E25.MirrorC"),sQuery(id+"F0.wireOp",EDGE,"E26.MirrorC"),sQuery(id+"F0.wireOp",EDGE,"E27.MirrorC"),sQuery(id+"F0.wireOp",EDGE,"E28.MirrorC"),sQuery(id+"F0.wireOp",EDGE,"E29.MirrorC"),sQuery(id+"F0.wireOp",EDGE,"E30.MirrorC"),sQuery(id+"F0.wireOp",EDGE,"E160.MirrorC"),sQuery(id+"F0.wireOp",EDGE,"E31.MirrorC"),sQuery(id+"F0.wireOp",EDGE,"E32.MirrorC"),sQuery(id+"F0.wireOp",EDGE,"E33.MirrorC"),sQuery(id+"F0.wireOp",EDGE,"E38.MirrorC"),sQuery(id+"F0.wireOp",EDGE,"E39.MirrorC"),sQuery(id+"F0.wireOp",EDGE,"E40.MirrorC"),sQuery(id+"F0.wireOp",EDGE,"E41.MirrorC"),sQuery(id+"F0.wireOp",EDGE,"E42.MirrorC"),sQuery(id+"F0.wireOp",EDGE,"E43.MirrorC"),sQuery(id+"F0.wireOp",EDGE,"E44.MirrorC"),sQuery(id+"F0.wireOp",EDGE,"E45.MirrorC"),sQuery(id+"F0.wireOp",EDGE,"E46.MirrorC"),sQuery(id+"F0.wireOp",EDGE,"E47.MirrorC"),sQuery(id+"F0.wireOp",EDGE,"E48.MirrorC"),sQuery(id+"F0.wireOp",EDGE,"E49.MirrorC"),sQuery(id+"F0.wireOp",EDGE,"E50.MirrorC"),sQuery(id+"F0.wireOp",EDGE,"E52.MirrorC"),sQuery(id+"F0.wireOp",EDGE,"E395.MirrorC"),sQuery(id+"F0.wireOp",EDGE,"E396.MirrorC"),sQuery(id+"F0.wireOp",EDGE,"E53.MirrorC"),sQuery(id+"F0.wireOp",EDGE,"E398.MirrorC"),sQuery(id+"F0.wireOp",EDGE,"E54.MirrorC"),sQuery(id+"F0.wireOp",EDGE,"E55.MirrorC"),sQuery(id+"F0.wireOp",EDGE,"E56.MirrorC"),sQuery(id+"F0.wireOp",EDGE,"E57.MirrorC"),sQuery(id+"F0.wireOp",EDGE,"E403.MirrorC"),sQuery(id+"F0.wireOp",EDGE,"E58.MirrorC"),sQuery(id+"F0.wireOp",EDGE,"E59.MirrorC"),sQuery(id+"F0.wireOp",EDGE,"E60.MirrorC"),sQuery(id+"F0.wireOp",EDGE,"E61.MirrorC"),sQuery(id+"F0.wireOp",EDGE,"E62.MirrorC"),sQuery(id+"F0.wireOp",EDGE,"E63.MirrorC"),sQuery(id+"F0.wireOp",EDGE,"E64.MirrorC"),sQuery(id+"F0.wireOp",EDGE,"E65.MirrorC"),sQuery(id+"F0.wireOp",EDGE,"E66.MirrorC"),sQuery(id+"F0.wireOp",EDGE,"E67.MirrorC"),sQuery(id+"F0.wireOp",EDGE,"E68.MirrorC"),sQuery(id+"F0.wireOp",EDGE,"E69.MirrorC"),sQuery(id+"F0.wireOp",EDGE,"E416.MirrorC"),sQuery(id+"F0.wireOp",EDGE,"E70.MirrorC"),sQuery(id+"F0.wireOp",EDGE,"E418.MirrorC"),sQuery(id+"F0.wireOp",EDGE,"E419.MirrorC"),sQuery(id+"F0.wireOp",EDGE,"E71.MirrorC"),sQuery(id+"F0.wireOp",EDGE,"E72.MirrorC"),sQuery(id+"F0.wireOp",EDGE,"E73.MirrorC"),sQuery(id+"F0.wireOp",EDGE,"E423.MirrorC"),sQuery(id+"F0.wireOp",EDGE,"E74.MirrorC"),sQuery(id+"F0.wireOp",EDGE,"E75.MirrorC"),sQuery(id+"F0.wireOp",EDGE,"E76.MirrorC"),sQuery(id+"F0.wireOp",EDGE,"E77.MirrorC"),sQuery(id+"F0.wireOp",EDGE,"E78.MirrorC"),sQuery(id+"F0.wireOp",EDGE,"E86.filletArc"),sQuery(id+"F0.wireOp",EDGE,"E87.filletArc"),sQuery(id+"F0.wireOp",EDGE,"E88"),sQuery(id+"F0.wireOp",EDGE,"E89"),sQuery(id+"F0.wireOp",EDGE,"E90"),sQuery(id+"F0.wireOp",EDGE,"E91")])]});
            hole(context, id + "F6", {"style" : HoleStyle.SIMPLE, "endStyle" : HoleEndStyle.BLIND, "holeDiameter" : 20 * mm, "majorDiameter" : 5 * mm, "holeDepth" : 40 * mm, "isTappedThrough" : true, "tappedDepth" : 12 * mm, "tapClearance" : 3, "locations" : qUnion([Q0, Q1]), "scope" : qUnion([Q2])});
        }
    });
